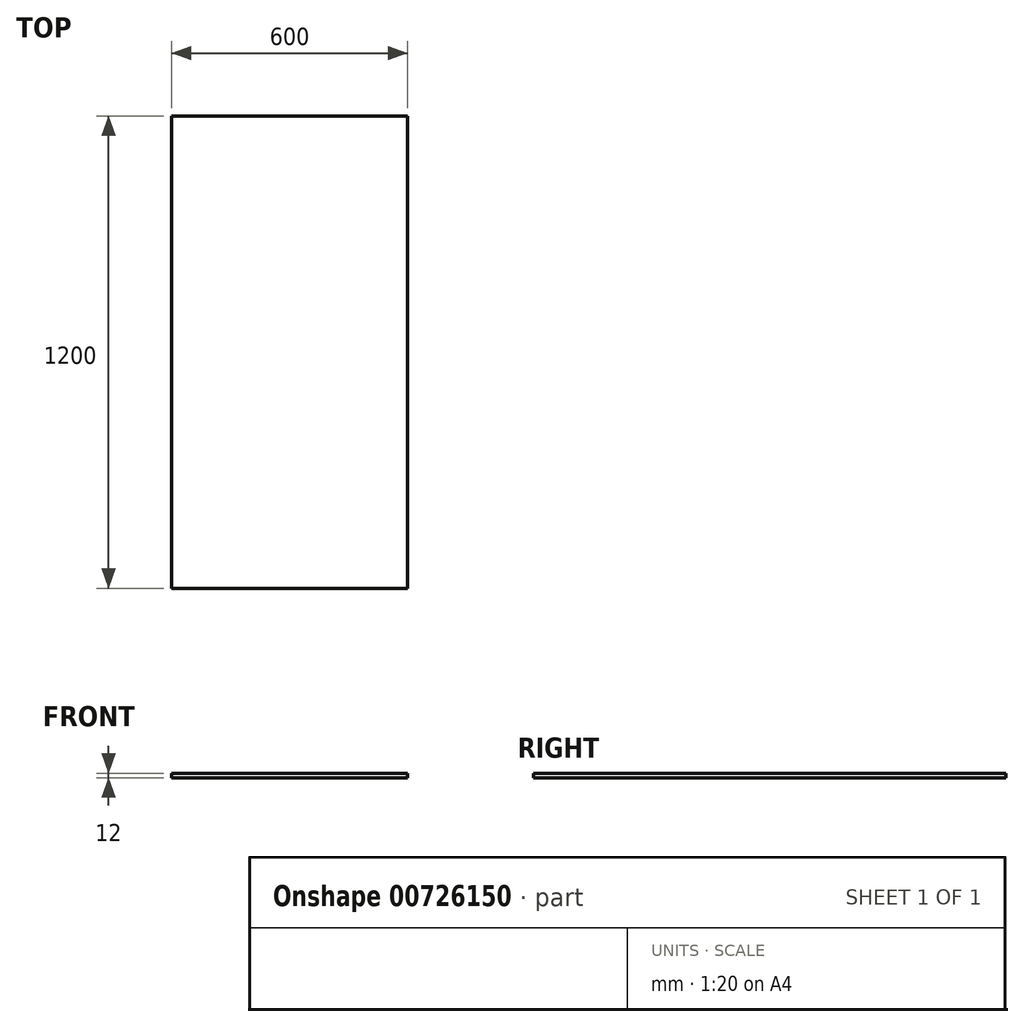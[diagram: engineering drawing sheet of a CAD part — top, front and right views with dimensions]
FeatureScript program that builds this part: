
annotation { "Feature Type Name" : "Feature", "Feature Type Description" : "" }
export const myFeature = defineFeature(function(context is Context, id is Id, definition is map)
    precondition{}
    {
        {
            var Q0;
            Q0=qCreatedBy(makeId("Top.planeOp"),FACE);
            var sketch = newSketch(context, id + "F0", { "sketchPlane" : qUnion([Q0])});
            skLineSegment(sketch, "E0.bottom", {"start": v(0, 0) * mm, "end": v(-600, 0) * mm});
            skLineSegment(sketch, "E0.top", {"start": v(0, 1200) * mm, "end": v(-600, 1200) * mm});
            skLineSegment(sketch, "E0.left", {"start": v(0, 0) * mm, "end": v(0, 1200) * mm});
            skLineSegment(sketch, "E0.right", {"start": v(-600, 0) * mm, "end": v(-600, 1200) * mm});
            skSolve(sketch);
        }
        {
            var Q0;
            Q0 = qSketchRegion(id + "F0", true);
            extrude(context, id + "F1", {"entities" : qUnion([Q0]), "depth" : 12 * mm, "offsetDistance" : 25 * mm});
        }
    });
